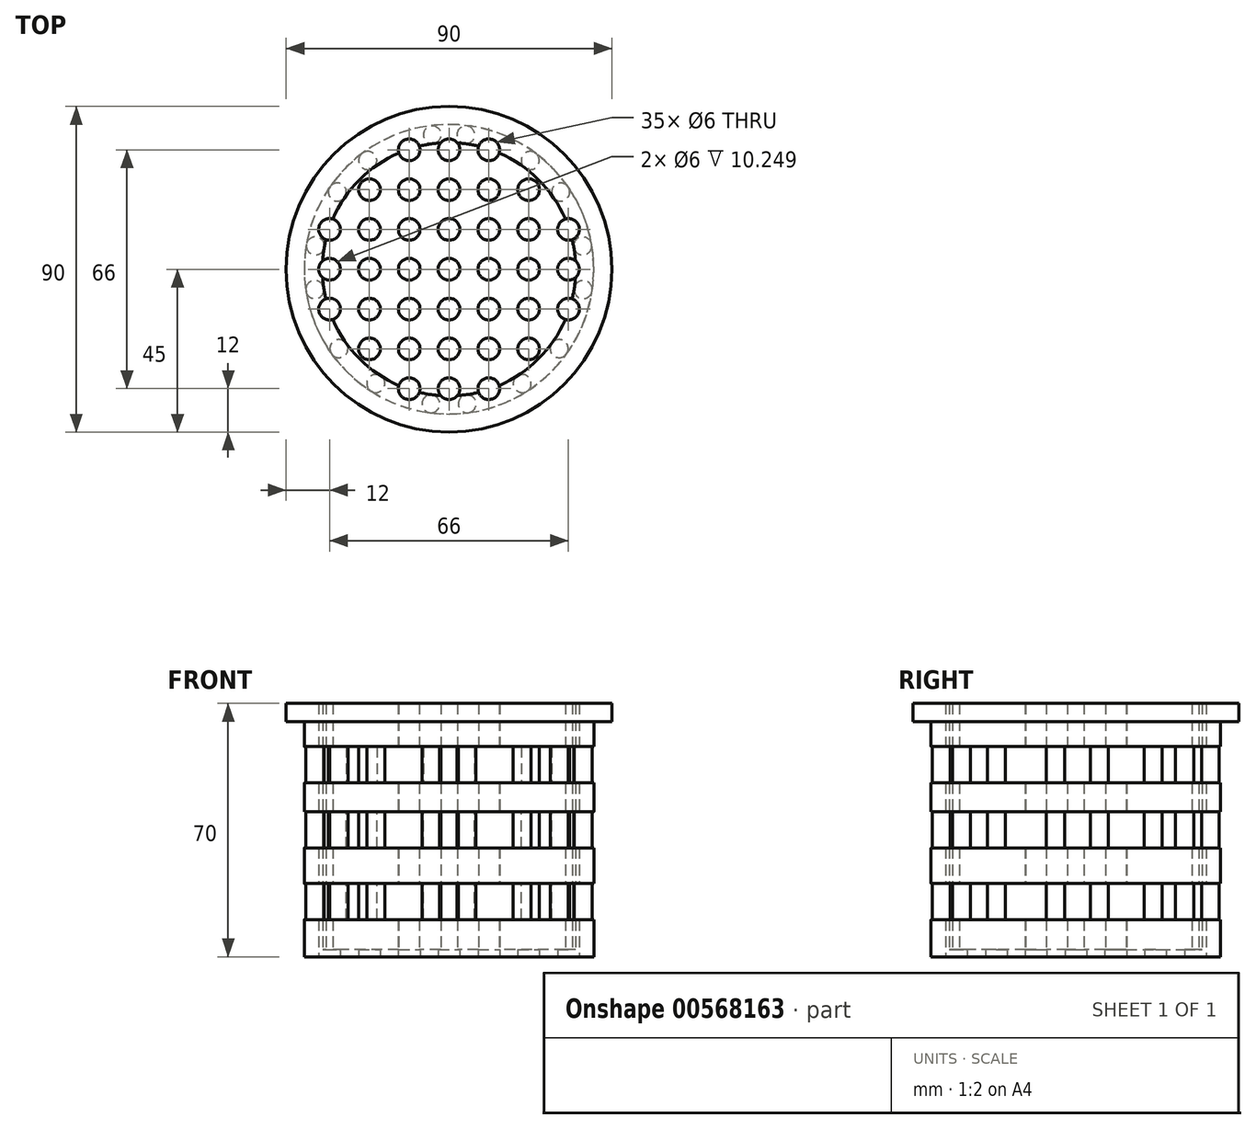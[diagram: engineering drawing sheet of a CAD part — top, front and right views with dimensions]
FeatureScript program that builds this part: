
annotation { "Feature Type Name" : "Feature", "Feature Type Description" : "" }
export const myFeature = defineFeature(function(context is Context, id is Id, definition is map)
    precondition{}
    {
        {
            var Q0;
            Q0=qCreatedBy(makeId("Top.planeOp"),FACE);
            var sketch = newSketch(context, id + "F0", { "sketchPlane" : qUnion([Q0])});
            skCircle(sketch, "E0", {"center": v(0, 0) * mm, "radius": 40 * mm});
            skSolve(sketch);
        }
        {
            var Q0;
            Q0=makeQuery(id+"F0.imprint","IMPRINT",FACE,{"disambiguationData":[TD([[makeQuery(id+"F0.imprint","IMPRINT",EDGE,{"derivedFrom":sQuery(id+"F0.wireOp",EDGE,"E0")}),1.0]])]});
            var Q1;
            Q1=sQuery(id+"F0.wireOp",EDGE,"E0");
            extrude(context, id + "F1", {"entities" : qUnion([Q0]), "surfaceEntities" : qUnion([Q1]), "oppositeDirection" : true, "depth" : 70 * mm, "offsetDistance" : 25 * mm});
        }
        {
            var Q0;
            Q0=makeQuery(id+"F1.opExtrude","CAP_FACE",FACE,{"disambiguationData":[OSD([sQuery(id+"F0.wireOp",EDGE,"E0")])],"isStart":true});
            var sketch = newSketch(context, id + "F2", { "sketchPlane" : qUnion([Q0])});
            skCircle(sketch, "E1", {"center": v(0, 0) * mm, "radius": 45 * mm});
            skSolve(sketch);
        }
        {
            var Q0;
            Q0 = qSketchRegion(id + "F2", true);
            extrude(context, id + "F3", {"entities" : qUnion([Q0]), "operationType" : NewBodyOperationType.ADD, "oppositeDirection" : true, "depth" : 5 * mm, "offsetDistance" : 25 * mm});
        }
        {
            var Q0;
            Q0=makeQuery(id+"F1.opExtrude","CAP_FACE",FACE,{"disambiguationData":[OSD([sQuery(id+"F0.wireOp",EDGE,"E0")])],"isStart":true});
            var sketch = newSketch(context, id + "F4", { "sketchPlane" : qUnion([Q0])});
            skCircle(sketch, "E2", {"center": v(0, 0) * mm, "radius": 35 * mm});
            skSolve(sketch);
        }
        {
            var Q0;
            Q0 = qSketchRegion(id + "F4", true);
            extrude(context, id + "F5", {"entities" : qUnion([Q0]), "operationType" : NewBodyOperationType.REMOVE, "oppositeDirection" : true, "depth" : 68 * mm, "offsetDistance" : 25 * mm});
        }
        {
            var Q0;
            Q0=makeQuery(id+"F1.opExtrude","CAP_FACE",FACE,{"disambiguationData":[OSD([sQuery(id+"F0.wireOp",EDGE,"E0")])],"isStart":false});
            var sketch = newSketch(context, id + "F6", { "sketchPlane" : qUnion([Q0])});
            skCircle(sketch, "E3", {"center": v(0, 0) * mm, "radius": 3 * mm});
            skCircle(sketch, "E4", {"center": v(0, 11) * mm, "radius": 3 * mm});
            skCircle(sketch, "E5", {"center": v(0, -11) * mm, "radius": 3 * mm});
            skCircle(sketch, "E6", {"center": v(-11, 0) * mm, "radius": 3 * mm});
            skCircle(sketch, "E7", {"center": v(11, 0) * mm, "radius": 3 * mm});
            skCircle(sketch, "E8", {"center": v(0, 22) * mm, "radius": 3 * mm});
            skCircle(sketch, "E9", {"center": v(-22, 0) * mm, "radius": 3 * mm});
            skCircle(sketch, "E10", {"center": v(22, 0) * mm, "radius": 3 * mm});
            skCircle(sketch, "E11", {"center": v(33, 0) * mm, "radius": 3 * mm});
            skCircle(sketch, "E12", {"center": v(0, 33) * mm, "radius": 3 * mm});
            skCircle(sketch, "E13", {"center": v(-33, 0) * mm, "radius": 3 * mm});
            skCircle(sketch, "E14", {"center": v(0, -22) * mm, "radius": 3 * mm});
            skCircle(sketch, "E15", {"center": v(0, -33) * mm, "radius": 3 * mm});
            skCircle(sketch, "E16", {"center": v(-11, -11) * mm, "radius": 3 * mm});
            skCircle(sketch, "E17", {"center": v(11, 11) * mm, "radius": 3 * mm});
            skCircle(sketch, "E18", {"center": v(-11, 11) * mm, "radius": 3 * mm});
            skCircle(sketch, "E19", {"center": v(11, -11) * mm, "radius": 3 * mm});
            skCircle(sketch, "E20", {"center": v(-22, 11) * mm, "radius": 3 * mm});
            skCircle(sketch, "E21", {"center": v(-11, 22) * mm, "radius": 3 * mm});
            skCircle(sketch, "E22", {"center": v(11, 22) * mm, "radius": 3 * mm});
            skCircle(sketch, "E23", {"center": v(22, 11) * mm, "radius": 3 * mm});
            skCircle(sketch, "E24", {"center": v(22, -11) * mm, "radius": 3 * mm});
            skCircle(sketch, "E25", {"center": v(11, -22) * mm, "radius": 3 * mm});
            skCircle(sketch, "E26", {"center": v(-22, -11) * mm, "radius": 3 * mm});
            skCircle(sketch, "E27", {"center": v(-11, -22) * mm, "radius": 3 * mm});
            skCircle(sketch, "E28", {"center": v(-22, 22) * mm, "radius": 3 * mm});
            skCircle(sketch, "E29", {"center": v(22, 22) * mm, "radius": 3 * mm});
            skCircle(sketch, "E30", {"center": v(22, -22) * mm, "radius": 3 * mm});
            skCircle(sketch, "E31", {"center": v(-22, -22) * mm, "radius": 3 * mm});
            skCircle(sketch, "E32", {"center": v(-33, 11) * mm, "radius": 3 * mm});
            skCircle(sketch, "E33", {"center": v(33, 11) * mm, "radius": 3 * mm});
            skCircle(sketch, "E34", {"center": v(33, -11) * mm, "radius": 3 * mm});
            skCircle(sketch, "E35", {"center": v(-11, -33) * mm, "radius": 3 * mm});
            skCircle(sketch, "E36", {"center": v(11, -33) * mm, "radius": 3 * mm});
            skCircle(sketch, "E37", {"center": v(-33, -11) * mm, "radius": 3 * mm});
            skCircle(sketch, "E38", {"center": v(-11, 33) * mm, "radius": 3 * mm});
            skCircle(sketch, "E39", {"center": v(11, 33) * mm, "radius": 3 * mm});
            skSolve(sketch);
        }
        {
            var Q0;
            Q0 = qSketchRegion(id + "F6", true);
            extrude(context, id + "F7", {"entities" : qUnion([Q0]), "operationType" : NewBodyOperationType.REMOVE, "endBound" : BoundingType.THROUGH_ALL, "oppositeDirection" : true, "depth" : 8 * mm, "offsetDistance" : 25 * mm});
        }
        {
            var Q0;
            Q0=qCreatedBy(makeId("Front.planeOp"),FACE);
            var sketch = newSketch(context, id + "F8", { "sketchPlane" : qUnion([Q0])});
            skLineSegment(sketch, "E40.bottom", {"start": v(41.16, -11.93) * mm, "end": v(-43.37, -11.93) * mm});
            skLineSegment(sketch, "E40.top", {"start": v(41.16, -21.93) * mm, "end": v(-43.37, -21.93) * mm});
            skLineSegment(sketch, "E40.left", {"start": v(41.16, -11.93) * mm, "end": v(41.16, -21.93) * mm});
            skLineSegment(sketch, "E40.right", {"start": v(-43.37, -11.93) * mm, "end": v(-43.37, -21.93) * mm});
            skLineSegment(sketch, "E41.bottom", {"start": v(41.16, -29.93) * mm, "end": v(-43.37, -29.93) * mm});
            skLineSegment(sketch, "E41.top", {"start": v(41.16, -39.93) * mm, "end": v(-43.37, -39.93) * mm});
            skLineSegment(sketch, "E41.left", {"start": v(41.16, -29.93) * mm, "end": v(41.16, -39.93) * mm});
            skLineSegment(sketch, "E41.right", {"start": v(-43.37, -29.93) * mm, "end": v(-43.37, -39.93) * mm});
            skLineSegment(sketch, "E42.bottom", {"start": v(41.16, -49.75) * mm, "end": v(-43.37, -49.75) * mm});
            skLineSegment(sketch, "E42.top", {"start": v(41.16, -59.75) * mm, "end": v(-43.37, -59.75) * mm});
            skLineSegment(sketch, "E42.left", {"start": v(41.16, -49.75) * mm, "end": v(41.16, -59.75) * mm});
            skLineSegment(sketch, "E42.right", {"start": v(-43.37, -49.75) * mm, "end": v(-43.37, -59.75) * mm});
            skSolve(sketch);
        }
        {
            var Q0;
            Q0 = qSketchRegion(id + "F8", true);
            extrude(context, id + "F9", {"entities" : qUnion([Q0]), "operationType" : NewBodyOperationType.REMOVE, "endBound" : BoundingType.THROUGH_ALL, "oppositeDirection" : true, "depth" : 25 * mm, "offsetDistance" : 25 * mm});
        }
        {
            var Q0;
            Q0 = qSketchRegion(id + "F8", true);
            extrude(context, id + "F10", {"entities" : qUnion([Q0]), "operationType" : NewBodyOperationType.REMOVE, "endBound" : BoundingType.THROUGH_ALL, "depth" : 25 * mm, "offsetDistance" : 25 * mm});
        }
        {
            var Q0;
            {var subQ0=sQuery(id+"F8.wireOp",EDGE,"E40.top");Q0=makeQuery(id+"F10.boolean.opBoolean","MERGE",FACE,{"derivedFrom":[makeQuery(id+"F9.boolean.opBoolean","COPY",FACE,{"derivedFrom":makeQuery(id+"F9.opExtrude","SWEPT_FACE",FACE,{"disambiguationData":[OSD([subQ0])]})}),makeQuery(id+"F10.opExtrude","SWEPT_FACE",FACE,{"disambiguationData":[OSD([subQ0])]})]});}
            var sketch = newSketch(context, id + "F11", { "sketchPlane" : qUnion([Q0])});
            skCircle(sketch, "E43", {"center": v(-30.43, -21.92) * mm, "radius": 2.5 * mm});
            skPoint(sketch, "E43.first.point", {"position": v(-32.45, -23.38) * mm});
            skPoint(sketch, "E43.second.point", {"position": v(-28.4, -20.46) * mm});
            skPoint(sketch, "E43.third.point", {"position": v(-32.45, -23.38) * mm});
            skCircle(sketch, "E44", {"center": v(-20.21, -31.59) * mm, "radius": 2.5 * mm});
            skCircle(sketch, "E45", {"center": v(-37.07, -5.64) * mm, "radius": 2.5 * mm});
            skPoint(sketch, "E45.first.point", {"position": v(-39.55, -6.01) * mm});
            skPoint(sketch, "E45.second.point", {"position": v(-34.6, -5.26) * mm});
            skPoint(sketch, "E45.third.point", {"position": v(-36.98, -8.14) * mm});
            skCircle(sketch, "E46", {"center": v(-36.94, 6.45) * mm, "radius": 2.5 * mm});
            skPoint(sketch, "E46.first.point", {"position": v(-39.4, 6.88) * mm});
            skPoint(sketch, "E46.second.point", {"position": v(-34.48, 6.02) * mm});
            skPoint(sketch, "E46.third.point", {"position": v(-36.75, 3.96) * mm});
            skCircle(sketch, "E47", {"center": v(-30.85, 21.32) * mm, "radius": 2.5 * mm});
            skPoint(sketch, "E47.first.point", {"position": v(-32.9, 22.74) * mm});
            skPoint(sketch, "E47.second.point", {"position": v(-28.8, 19.9) * mm});
            skPoint(sketch, "E47.third.point", {"position": v(-31.78, 19) * mm});
            skCircle(sketch, "E48", {"center": v(-22.44, 30.04) * mm, "radius": 2.5 * mm});
            skPoint(sketch, "E48.first.point", {"position": v(-23.94, 32.05) * mm});
            skPoint(sketch, "E48.second.point", {"position": v(-20.95, 28.04) * mm});
            skPoint(sketch, "E48.third.point", {"position": v(-24.12, 28.19) * mm});
            skCircle(sketch, "E49", {"center": v(-4.63, 37.16) * mm, "radius": 2.45 * mm});
            skPoint(sketch, "E49.second.point", {"position": v(-4.33, 34.73) * mm});
            skPoint(sketch, "E49.third.point", {"position": v(-7.08, 37.02) * mm});
            skCircle(sketch, "E50", {"center": v(-5.02, -37.21) * mm, "radius": 2.45 * mm});
            skPoint(sketch, "E50.first.point", {"position": v(-5.35, -39.64) * mm});
            skPoint(sketch, "E50.third.point", {"position": v(-7.32, -36.36) * mm});
            skSolve(sketch);
        }
        {
            var Q0;
            Q0 = qSketchRegion(id + "F11", true);
            extrude(context, id + "F12", {"entities" : qUnion([Q0]), "depth" : 13 * mm, "offsetDistance" : 25 * mm});
        }
        {
            var Q0;
            Q0=makeQuery(id+"F12.opExtrude","SWEPT_BODY",BODY,{"disambiguationData":[OSD([sQuery(id+"F11.wireOp",EDGE,"E44")])]});
            var Q1;
            Q1=makeQuery(id+"F12.opExtrude","SWEPT_BODY",BODY,{"disambiguationData":[OSD([sQuery(id+"F11.wireOp",EDGE,"E43")])]});
            var Q2;
            Q2=makeQuery(id+"F12.opExtrude","SWEPT_BODY",BODY,{"disambiguationData":[OSD([sQuery(id+"F11.wireOp",EDGE,"E45")])]});
            var Q3;
            Q3=makeQuery(id+"F12.opExtrude","SWEPT_BODY",BODY,{"disambiguationData":[OSD([sQuery(id+"F11.wireOp",EDGE,"E46")])]});
            var Q4;
            Q4=makeQuery(id+"F12.opExtrude","SWEPT_BODY",BODY,{"disambiguationData":[OSD([sQuery(id+"F11.wireOp",EDGE,"E47")])]});
            var Q5;
            Q5=makeQuery(id+"F12.opExtrude","SWEPT_BODY",BODY,{"disambiguationData":[OSD([sQuery(id+"F11.wireOp",EDGE,"E48")])]});
            var Q6;
            Q6=makeQuery(id+"F12.opExtrude","SWEPT_BODY",BODY,{"disambiguationData":[OSD([sQuery(id+"F11.wireOp",EDGE,"E49")])]});
            var Q7;
            Q7=makeQuery(id+"F12.opExtrude","SWEPT_BODY",BODY,{"disambiguationData":[OSD([sQuery(id+"F11.wireOp",EDGE,"E50")])]});
            var Q8;
            Q8=qCreatedBy(makeId("Right.planeOp"),FACE);
            mirror(context, id + "F13", {"operationType" : NewBodyOperationType.ADD, "entities" : qUnion([Q0, Q1, Q2, Q3, Q4, Q5, Q6, Q7]), "mirrorPlane" : qUnion([Q8])});
        }
        {
            var Q0;
            {var subQ0=sQuery(id+"F8.wireOp",EDGE,"E41.bottom");Q0=makeQuery(id+"F10.boolean.opBoolean","MERGE",FACE,{"derivedFrom":[makeQuery(id+"F9.boolean.opBoolean","COPY",FACE,{"derivedFrom":makeQuery(id+"F9.opExtrude","SWEPT_FACE",FACE,{"disambiguationData":[OSD([subQ0])]})}),makeQuery(id+"F10.opExtrude","SWEPT_FACE",FACE,{"disambiguationData":[OSD([subQ0])]})]});}
            var sketch = newSketch(context, id + "F14", { "sketchPlane" : qUnion([Q0])});
            skCircle(sketch, "E51", {"center": v(-5.02, 37.21) * mm, "radius": 2.45 * mm});
            skPoint(sketch, "E51.second.point", {"position": v(-7.33, 36.4) * mm});
            skCircle(sketch, "E52", {"center": v(-20.21, 31.59) * mm, "radius": 2.5 * mm});
            skPoint(sketch, "E52.first.point", {"position": v(-21.56, 33.7) * mm});
            skPoint(sketch, "E52.second.point", {"position": v(-18.23, 33.1) * mm});
            skPoint(sketch, "E52.third.point", {"position": v(-18.86, 29.48) * mm});
            skCircle(sketch, "E53", {"center": v(-30.43, 21.92) * mm, "radius": 2.5 * mm});
            skCircle(sketch, "E54", {"center": v(-37.07, 5.64) * mm, "radius": 2.5 * mm});
            skCircle(sketch, "E55", {"center": v(-36.94, -6.45) * mm, "radius": 2.5 * mm});
            skCircle(sketch, "E56", {"center": v(-30.85, -21.32) * mm, "radius": 2.5 * mm});
            skCircle(sketch, "E57", {"center": v(-22.44, -30.04) * mm, "radius": 2.5 * mm});
            skCircle(sketch, "E58", {"center": v(-4.63, -37.16) * mm, "radius": 2.45 * mm});
            skSolve(sketch);
        }
        {
            var Q0;
            Q0 = qSketchRegion(id + "F14", true);
            extrude(context, id + "F15", {"entities" : qUnion([Q0]), "depth" : 13 * mm, "offsetDistance" : 25 * mm});
        }
        {
            var Q0;
            Q0=makeQuery(id+"F15.opExtrude","SWEPT_BODY",BODY,{"disambiguationData":[OSD([sQuery(id+"F14.wireOp",EDGE,"E53")])]});
            var Q1;
            Q1=makeQuery(id+"F15.opExtrude","SWEPT_BODY",BODY,{"disambiguationData":[OSD([sQuery(id+"F14.wireOp",EDGE,"E52")])]});
            var Q2;
            Q2=makeQuery(id+"F15.opExtrude","SWEPT_BODY",BODY,{"disambiguationData":[OSD([sQuery(id+"F14.wireOp",EDGE,"E51")])]});
            var Q3;
            Q3=makeQuery(id+"F15.opExtrude","SWEPT_BODY",BODY,{"disambiguationData":[OSD([sQuery(id+"F14.wireOp",EDGE,"E54")])]});
            var Q4;
            Q4=makeQuery(id+"F15.opExtrude","SWEPT_BODY",BODY,{"disambiguationData":[OSD([sQuery(id+"F14.wireOp",EDGE,"E55")])]});
            var Q5;
            Q5=makeQuery(id+"F15.opExtrude","SWEPT_BODY",BODY,{"disambiguationData":[OSD([sQuery(id+"F14.wireOp",EDGE,"E56")])]});
            var Q6;
            Q6=makeQuery(id+"F15.opExtrude","SWEPT_BODY",BODY,{"disambiguationData":[OSD([sQuery(id+"F14.wireOp",EDGE,"E57")])]});
            var Q7;
            Q7=makeQuery(id+"F15.opExtrude","SWEPT_BODY",BODY,{"disambiguationData":[OSD([sQuery(id+"F14.wireOp",EDGE,"E58")])]});
            var Q8;
            Q8=qCreatedBy(makeId("Right.planeOp"),FACE);
            mirror(context, id + "F16", {"operationType" : NewBodyOperationType.ADD, "entities" : qUnion([Q0, Q1, Q2, Q3, Q4, Q5, Q6, Q7]), "mirrorPlane" : qUnion([Q8])});
        }
        {
            var Q0;
            {var subQ0=sQuery(id+"F8.wireOp",EDGE,"E42.bottom");Q0=makeQuery(id+"F10.boolean.opBoolean","MERGE",FACE,{"derivedFrom":[makeQuery(id+"F9.boolean.opBoolean","COPY",FACE,{"derivedFrom":makeQuery(id+"F9.opExtrude","SWEPT_FACE",FACE,{"disambiguationData":[OSD([subQ0])]})}),makeQuery(id+"F10.opExtrude","SWEPT_FACE",FACE,{"disambiguationData":[OSD([subQ0])]})]});}
            var sketch = newSketch(context, id + "F17", { "sketchPlane" : qUnion([Q0])});
            skCircle(sketch, "E59", {"center": v(-5.02, 37.21) * mm, "radius": 2.45 * mm});
            skCircle(sketch, "E60", {"center": v(-20.21, 31.59) * mm, "radius": 2.5 * mm});
            skCircle(sketch, "E61", {"center": v(-30.43, 21.92) * mm, "radius": 2.5 * mm});
            skCircle(sketch, "E62", {"center": v(-37.07, 5.64) * mm, "radius": 2.5 * mm});
            skCircle(sketch, "E63", {"center": v(-36.94, -6.45) * mm, "radius": 2.5 * mm});
            skCircle(sketch, "E64", {"center": v(-30.85, -21.32) * mm, "radius": 2.5 * mm});
            skCircle(sketch, "E65", {"center": v(-22.44, -30.04) * mm, "radius": 2.5 * mm});
            skCircle(sketch, "E66", {"center": v(-4.63, -37.16) * mm, "radius": 2.45 * mm});
            skSolve(sketch);
        }
        {
            var Q0;
            Q0 = qSketchRegion(id + "F17", true);
            extrude(context, id + "F18", {"entities" : qUnion([Q0]), "depth" : 13 * mm, "offsetDistance" : 25 * mm});
        }
        {
            var Q0;
            Q0=makeQuery(id+"F18.opExtrude","SWEPT_BODY",BODY,{"disambiguationData":[OSD([sQuery(id+"F17.wireOp",EDGE,"E59")])]});
            var Q1;
            Q1=makeQuery(id+"F18.opExtrude","SWEPT_BODY",BODY,{"disambiguationData":[OSD([sQuery(id+"F17.wireOp",EDGE,"E60")])]});
            var Q2;
            Q2=makeQuery(id+"F18.opExtrude","SWEPT_BODY",BODY,{"disambiguationData":[OSD([sQuery(id+"F17.wireOp",EDGE,"E61")])]});
            var Q3;
            Q3=makeQuery(id+"F18.opExtrude","SWEPT_BODY",BODY,{"disambiguationData":[OSD([sQuery(id+"F17.wireOp",EDGE,"E62")])]});
            var Q4;
            Q4=makeQuery(id+"F18.opExtrude","SWEPT_BODY",BODY,{"disambiguationData":[OSD([sQuery(id+"F17.wireOp",EDGE,"E63")])]});
            var Q5;
            Q5=makeQuery(id+"F18.opExtrude","SWEPT_BODY",BODY,{"disambiguationData":[OSD([sQuery(id+"F17.wireOp",EDGE,"E64")])]});
            var Q6;
            Q6=makeQuery(id+"F18.opExtrude","SWEPT_BODY",BODY,{"disambiguationData":[OSD([sQuery(id+"F17.wireOp",EDGE,"E65")])]});
            var Q7;
            Q7=makeQuery(id+"F18.opExtrude","SWEPT_BODY",BODY,{"disambiguationData":[OSD([sQuery(id+"F17.wireOp",EDGE,"E66")])]});
            var Q8;
            Q8=qCreatedBy(makeId("Right.planeOp"),FACE);
            mirror(context, id + "F19", {"operationType" : NewBodyOperationType.ADD, "entities" : qUnion([Q0, Q1, Q2, Q3, Q4, Q5, Q6, Q7]), "mirrorPlane" : qUnion([Q8])});
        }
    });
